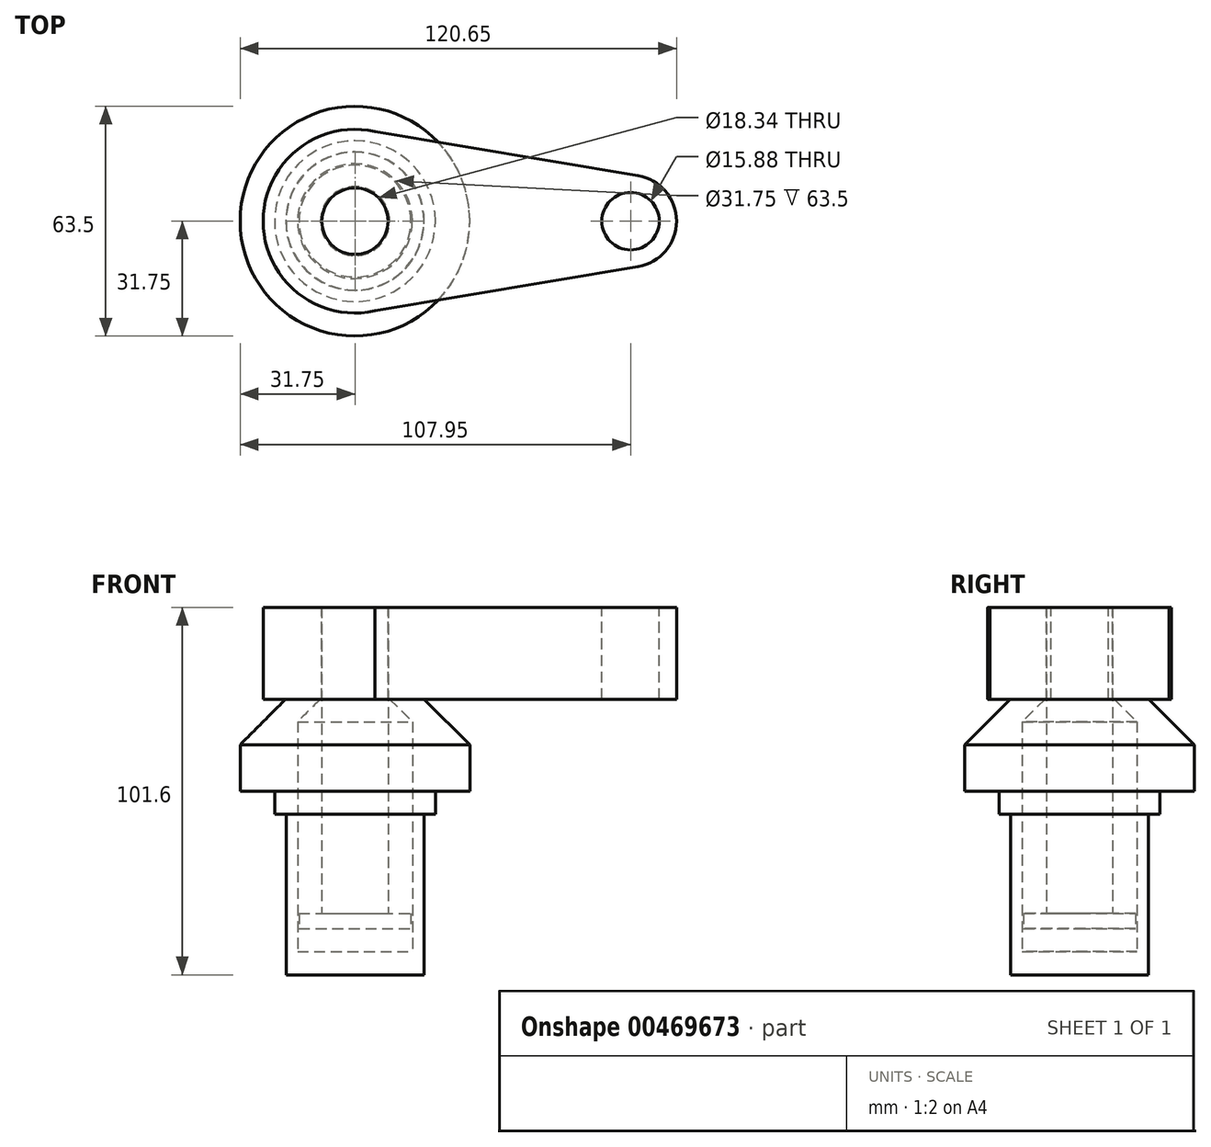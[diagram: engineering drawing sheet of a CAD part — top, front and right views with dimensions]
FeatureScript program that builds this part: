
annotation { "Feature Type Name" : "Feature", "Feature Type Description" : "" }
export const myFeature = defineFeature(function(context is Context, id is Id, definition is map)
    precondition{}
    {
        {
            var Q0;
            Q0=qCreatedBy(makeId("Front.planeOp"),FACE);
            var sketch = newSketch(context, id + "F0", { "sketchPlane" : qUnion([Q0])});
            skLineSegment(sketch, "E0", {"start": v(0, 76.2) * mm, "end": v(19.15, 76.2) * mm});
            skLineSegment(sketch, "E1", {"start": v(19.15, 76.2) * mm, "end": v(31.75, 63.6) * mm});
            skLineSegment(sketch, "E2", {"start": v(31.75, 63.6) * mm, "end": v(31.75, 50.8) * mm});
            skLineSegment(sketch, "E3", {"start": v(31.75, 50.8) * mm, "end": v(22.23, 50.8) * mm});
            skLineSegment(sketch, "E4", {"start": v(22.23, 50.8) * mm, "end": v(22.23, 44.45) * mm});
            skLineSegment(sketch, "E5", {"start": v(22.23, 44.45) * mm, "end": v(19.05, 44.45) * mm});
            skLineSegment(sketch, "E6", {"start": v(19.05, 44.45) * mm, "end": v(19.05, 0) * mm});
            skLineSegment(sketch, "E7", {"start": v(19.05, 0) * mm, "end": v(0, 0) * mm});
            skLineSegment(sketch, "E8", {"start": v(0, 0) * mm, "end": v(0, 76.2) * mm});
            skLineSegment(sketch, "E9", {"start": v(9.58, 76.2) * mm, "end": v(15.88, 69.99) * mm});
            skLineSegment(sketch, "E10", {"start": v(15.88, 69.99) * mm, "end": v(15.88, 6.49) * mm});
            skLineSegment(sketch, "E11", {"start": v(15.88, 6.49) * mm, "end": v(0, 6.49) * mm});
            skLineSegment(sketch, "E12", {"start": v(0, 76.2) * mm, "end": v(0, 88.42) * mm, "construction": true});
            skLineSegment(sketch, "E13", {"start": v(0, 76.2) * mm, "end": v(0, 101.6) * mm});
            skLineSegment(sketch, "E14", {"start": v(0, 101.6) * mm, "end": v(9.17, 101.6) * mm});
            skLineSegment(sketch, "E15", {"start": v(9.17, 101.6) * mm, "end": v(9.17, 16.98) * mm});
            skLineSegment(sketch, "E16", {"start": v(9.17, 16.98) * mm, "end": v(15.47, 16.98) * mm});
            skLineSegment(sketch, "E17", {"start": v(15.47, 16.98) * mm, "end": v(15.47, 12.84) * mm});
            skLineSegment(sketch, "E18", {"start": v(15.47, 12.84) * mm, "end": v(0, 12.84) * mm});
            skLineSegment(sketch, "E19", {"start": v(0, 76.2) * mm, "end": v(0, 132.36) * mm, "construction": true});
            skSolve(sketch);
        }
        {
            var Q0;
            {var subQ4=sQuery(id+"F0.wireOp",EDGE,"E1");Q0=makeQuery(id+"F0.imprint","IMPRINT",FACE,{"disambiguationData":[TD([[makeQuery(id+"F0.imprint","IMPRINT",EDGE,{"derivedFrom":subQ4}),-1.0]])]});}
            var Q1;
            Q1=sQuery(id+"F0.wireOp",EDGE,"E12");
            revolve(context, id + "F1", {"entities" : qUnion([Q0]), "axis" : qUnion([Q1]), "revolveType" : RevolveType.FULL});
        }
        {
            var Q0;
            {var subQ0=sQuery(id+"F0.wireOp",EDGE,"E16");Q0=makeQuery(id+"F0.imprint","IMPRINT",FACE,{"disambiguationData":[TD([[makeQuery(id+"F0.imprint","IMPRINT",EDGE,{"derivedFrom":subQ0}),-1.0]])]});}
            var Q1;
            {var subQ0=sQuery(id+"F0.wireOp",EDGE,"E13");Q1=makeQuery(id+"F0.imprint","IMPRINT",FACE,{"disambiguationData":[TD([[makeQuery(id+"F0.imprint","IMPRINT",EDGE,{"derivedFrom":subQ0}),-1.0]])]});}
            var Q2;
            Q2=sQuery(id+"F0.wireOp",EDGE,"E19");
            revolve(context, id + "F2", {"operationType" : NewBodyOperationType.ADD, "entities" : qUnion([Q0, Q1]), "axis" : qUnion([Q2]), "revolveType" : RevolveType.FULL});
        }
        {
            var Q0;
            Q0=makeQuery(id+"F2.opRevolve","SWEPT_FACE",FACE,{"disambiguationData":[OSD([sQuery(id+"F0.wireOp",EDGE,"E14")])]});
            var sketch = newSketch(context, id + "F3", { "sketchPlane" : qUnion([Q0])});
            skArc(sketch, "E20", {"start": v(5.55, 24.79) * mm, "mid": v(-25.4, 0) * mm, "end": v(5.55, -24.79) * mm});
            skArc(sketch, "E21", {"start": v(78.31, -12.52) * mm, "mid": v(88.9, 0) * mm, "end": v(78.31, 12.52) * mm});
            skLineSegment(sketch, "E22", {"start": v(5.55, 24.79) * mm, "end": v(78.31, 12.52) * mm});
            skLineSegment(sketch, "E23.MirrorCS", {"start": v(5.55, -24.79) * mm, "end": v(78.31, -12.52) * mm});
            skCircle(sketch, "E24.0", {"center": v(0, 0) * mm, "radius": 9.17 * mm});
            skCircle(sketch, "E25", {"center": v(76.2, 0) * mm, "radius": 7.94 * mm});
            skSolve(sketch);
        }
        {
            var Q0;
            Q0 = qSketchRegion(id + "F3", true);
            var Q1;
            Q1=makeQuery(id+"F1.opRevolve","SWEPT_FACE",FACE,{"disambiguationData":[OSD([sQuery(id+"F0.wireOp",EDGE,"E0")])]});
            var Q2;
            Q2=makeQuery(id+"F1.opRevolve","SWEPT_BODY",BODY,{"disambiguationData":[OSD([sQuery(id+"F0.wireOp",EDGE,"E0"),sQuery(id+"F0.wireOp",EDGE,"E1"),sQuery(id+"F0.wireOp",EDGE,"E2"),sQuery(id+"F0.wireOp",EDGE,"E3"),sQuery(id+"F0.wireOp",EDGE,"E4"),sQuery(id+"F0.wireOp",EDGE,"E5"),sQuery(id+"F0.wireOp",EDGE,"E6"),sQuery(id+"F0.wireOp",EDGE,"E7"),sQuery(id+"F0.wireOp",EDGE,"E8"),sQuery(id+"F0.wireOp",EDGE,"E9"),sQuery(id+"F0.wireOp",EDGE,"E10"),sQuery(id+"F0.wireOp",EDGE,"E11")])]});
            extrude(context, id + "F4", {"entities" : qUnion([Q0]), "endBound" : BoundingType.UP_TO_SURFACE, "oppositeDirection" : true, "endBoundEntityFace" : qUnion([Q1]), "endBoundEntityBody" : qUnion([Q2]), "depth" : 25.4 * mm});
        }
    });
